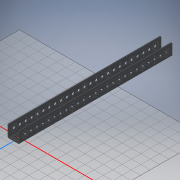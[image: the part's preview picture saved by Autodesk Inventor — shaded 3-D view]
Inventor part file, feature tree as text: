
AUTODESK INVENTOR PART (.ipt)
format: ipt  version: 2022 (Build 260153000, 153)  size: 641,024 bytes
history: native  units: in
note: dims shown in document units (in); Inventor stores cm internally (conversion verified against a paired STEP export)
features: other x216, plane x2, imported_body x1
ambient origin geometry x8: Origin, YZ Plane, XZ Plane, XY Plane, X Axis, Y Axis, Z Axis, Center Point
bodies: Body1 (feature_tree)
feature tree (219):
  other  "tetrix_739069_2012"
  other  "tetrix_739069_20121"
  other  "A_1"
  other  "A_78"
  other  "A_79"
  other  "A_80"
  other  "A_81"
  other  "A_82"
  other  "A_83"
  other  "A_84"
  other  "A_85"
  other  "A_27"
  other  "A_86"
  other  "A_87"
  other  "A_88"
  other  "A_89"
  other  "A_90"
  other  "A_91"
  other  "A_92"
  other  "A_93"
  other  "A_119"
  other  "A_120"
  other  "A_121"
  other  "A_122"
  other  "A_123"
  other  "A_124"
  other  "A_125"
  other  "A_126"
  other  "A_127"
  other  "A_149"
  other  "A_150"
  other  "A_151"
  other  "A_152"
  other  "A_153"
  other  "A_154"
  other  "A_155"
  other  "A_156"
  other  "A_157"
  other  "A_158"
  other  "A_159"
  other  "A_160"
  other  "A_161"
  other  "A_162"
  other  "A_163"
  other  "A_164"
  other  "A_165"
  other  "A_166"
  other  "Work Axis46"
  other  "Work Axis47"
  other  "Work Axis48"
  other  "Work Axis49"
  other  "Work Axis50"
  other  "Work Axis51"
  other  "Work Axis52"
  other  "Work Axis53"
  other  "Work Axis54"
  other  "Work Axis55"
  other  "Work Axis56"
  other  "Work Axis57"
  other  "Work Axis58"
  other  "Work Axis59"
  other  "Work Axis60"
  other  "Work Axis61"
  other  "Work Axis62"
  other  "Work Axis63"
  other  "A_18"
  other  "A_94"
  other  "A_95"
  other  "A_96"
  other  "A_97"
  other  "A_98"
  other  "A_99"
  other  "A_100"
  other  "A_101"
  other  "A_31"
  other  "A_102"
  other  "A_103"
  other  "A_104"
  other  "A_105"
  other  "A_106"
  other  "A_107"
  other  "A_108"
  other  "A_109"
  other  "A_128"
  other  "A_129"
  other  "A_130"
  other  "A_131"
  other  "A_132"
  other  "A_133"
  other  "A_134"
  other  "A_135"
  other  "A_136"
  other  "A_1283"
  other  "A_1284"
  other  "A_1285"
  other  "A_1286"
  other  "A_1287"
  other  "A_1288"
  other  "A_1289"
  other  "A_1290"
  other  "A_1291"
  other  "A_1292"
  other  "A_1293"
  other  "A_1294"
  other  "A_1295"
  other  "A_1296"
  other  "A_1297"
  other  "A_1298"
  other  "A_1299"
  other  "A_1300"
  other  "Work Axis109"
  other  "Work Axis110"
  other  "Work Axis111"
  other  "Work Axis112"
  other  "Work Axis113"
  other  "Work Axis114"
  other  "Work Axis115"
  other  "Work Axis116"
  other  "Work Axis117"
  other  "Work Axis118"
  other  "Work Axis119"
  other  "Work Axis120"
  other  "Work Axis121"
  other  "Work Axis122"
  other  "Work Axis123"
  other  "Work Axis124"
  other  "Work Axis125"
  other  "Work Axis126"
  other  "A_77"
  other  "A_110"
  other  "A_111"
  other  "A_112"
  other  "A_113"
  other  "A_139"
  other  "A_140"
  other  "A_141"
  other  "A_142"
  other  "A_143"
  other  "A_2421"
  other  "A_2422"
  other  "A_2423"
  other  "A_2424"
  other  "A_2425"
  other  "A_2426"
  other  "A_2427"
  other  "A_2428"
  other  "A_2429"
  other  "A_2430"
  other  "A_2449"
  other  "A_2450"
  other  "A_2451"
  other  "A_2452"
  other  "A_2453"
  other  "A_2454"
  other  "A_2455"
  other  "A_2456"
  other  "A_2457"
  other  "A_2458"
  other  "A_114"
  other  "A_115"
  other  "A_116"
  other  "A_117"
  other  "A_118"
  other  "A_144"
  other  "A_145"
  other  "A_146"
  other  "A_147"
  other  "A_148"
  other  "A_2431"
  other  "A_2432"
  other  "A_2433"
  other  "A_2434"
  other  "A_2435"
  other  "A_2436"
  other  "A_2437"
  other  "A_2438"
  other  "A_2439"
  other  "A_2440"
  other  "A_2459"
  other  "A_2460"
  other  "A_2461"
  other  "A_2462"
  other  "A_2463"
  other  "A_2464"
  other  "A_2465"
  other  "A_2466"
  other  "A_2467"
  other  "A_2468"
  other  "A_75"
  other  "A_76"
  other  "A_137"
  other  "A_138"
  other  "A_2441"
  other  "A_2442"
  other  "A_2443"
  other  "A_2444"
  other  "A_2469"
  other  "A_2470"
  other  "A_2471"
  other  "A_2472"
  other  "A_2417"
  other  "A_2418"
  other  "A_2419"
  other  "A_2420"
  other  "A_2445"
  other  "A_2446"
  other  "A_2447"
  other  "A_2448"
  other  "A_2473"
  other  "A_2474"
  other  "A_2475"
  other  "A_2476"
  other  "FRONT"
  other  "TOP"
  other  "RIGHT"
  other  "DTM1"
  plane  "Work Plane5"
  plane  "Work Plane6"
  imported_body  "Base1"
